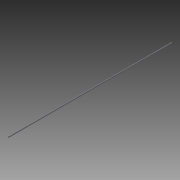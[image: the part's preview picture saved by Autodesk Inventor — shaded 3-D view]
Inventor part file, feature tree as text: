
AUTODESK INVENTOR PART (.ipt)
format: ipt  version: 2013 (Build 170138000, 138)  size: 83,968 bytes
history: native  units: in
note: dims shown in document units (in); Inventor stores cm internally (conversion verified against a paired STEP export)
features: other x2, plane x1, extrude x1, sketch x1
ambient origin geometry x8: Origin, YZ Plane, XZ Plane, XY Plane, X Axis, Y Axis, Z Axis, Center Point
feature tree (5):
  other  "Table"
  other  "vee-track-01"
  plane  "Work Plane1"
  extrude  "Extrusion1"  [1 undecoded]
  sketch  "Sketch1"  dims[d1=0.0in]
note: 1 required parameter value undecoded (feature->parameter linkage not recoverable at this tier; creation-order binding heuristic only, values carry confidence <= 0.55)
